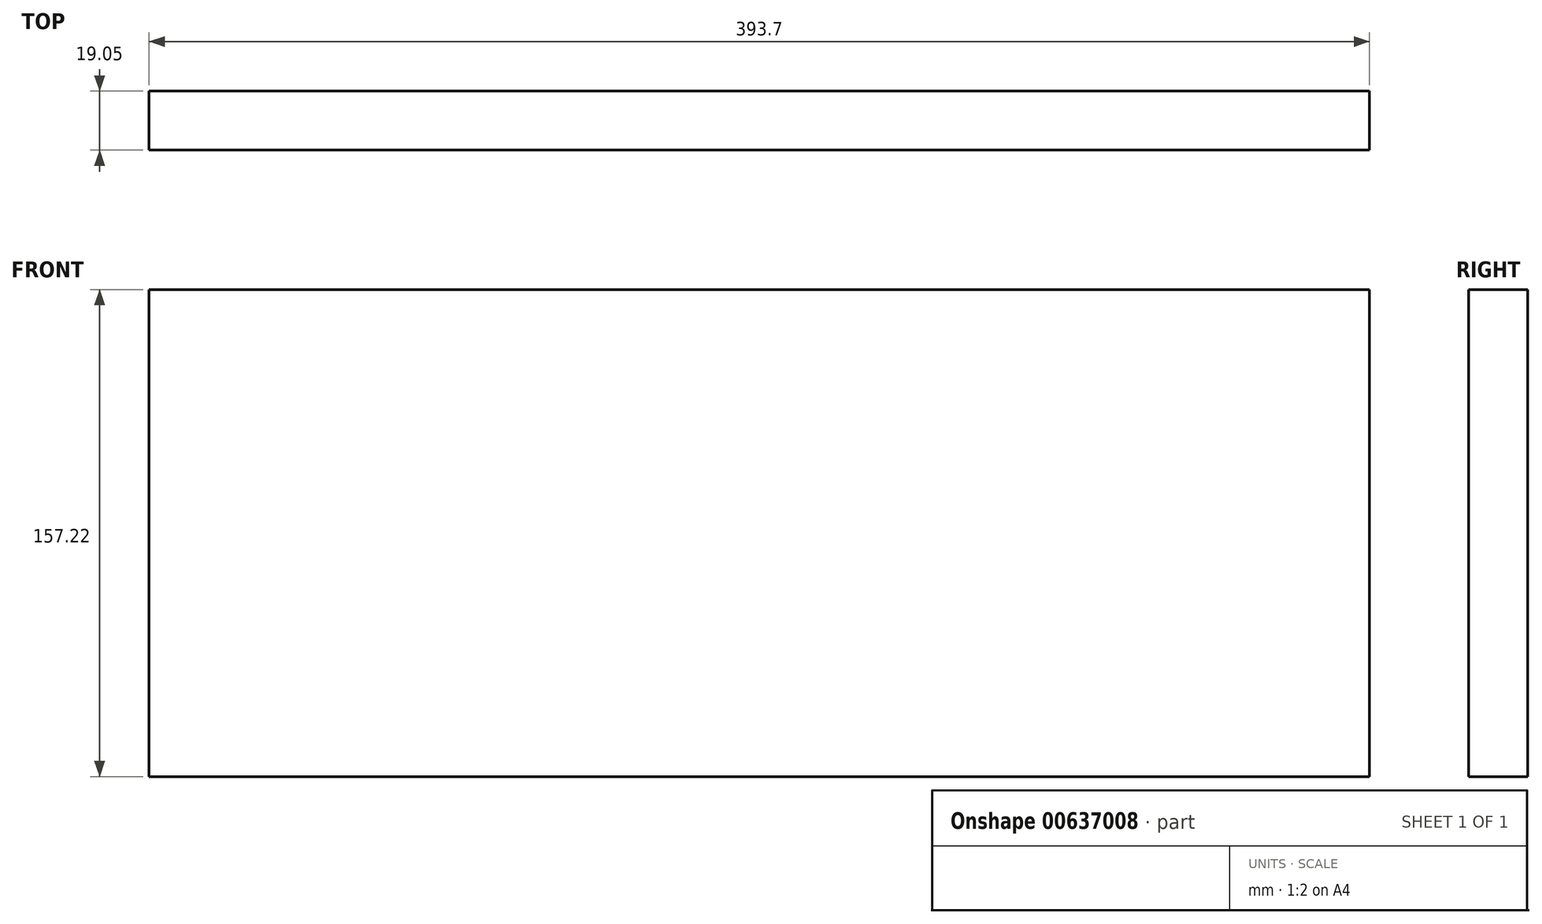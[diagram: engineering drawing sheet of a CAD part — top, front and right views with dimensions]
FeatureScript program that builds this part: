
annotation { "Feature Type Name" : "Feature", "Feature Type Description" : "" }
export const myFeature = defineFeature(function(context is Context, id is Id, definition is map)
    precondition{}
    {
        {
            var Q0;
            Q0=qCreatedBy(makeId("Front.planeOp"),FACE);
            var sketch = newSketch(context, id + "F0", { "sketchPlane" : qUnion([Q0])});
            skLineSegment(sketch, "E0.bottom", {"start": v(196.85, 78.61) * mm, "end": v(-196.85, 78.61) * mm});
            skLineSegment(sketch, "E0.top", {"start": v(196.85, -78.61) * mm, "end": v(-196.85, -78.61) * mm});
            skLineSegment(sketch, "E0.left", {"start": v(196.85, 78.61) * mm, "end": v(196.85, -78.61) * mm});
            skLineSegment(sketch, "E0.right", {"start": v(-196.85, 78.61) * mm, "end": v(-196.85, -78.61) * mm});
            skPoint(sketch, "E0.middle", {"position": v(0, 0) * mm});
            skSolve(sketch);
        }
        {
            var Q0;
            Q0=makeQuery(id+"F0.imprint","IMPRINT",FACE,{"disambiguationData":[TD([[makeQuery(id+"F0.imprint","IMPRINT",EDGE,{"derivedFrom":sQuery(id+"F0.wireOp",EDGE,"E0.bottom")}),1.0]])]});
            extrude(context, id + "F1", {"entities" : qUnion([Q0]), "depth" : 19.05 * mm, "offsetDistance" : 25.4 * mm});
        }
    });
